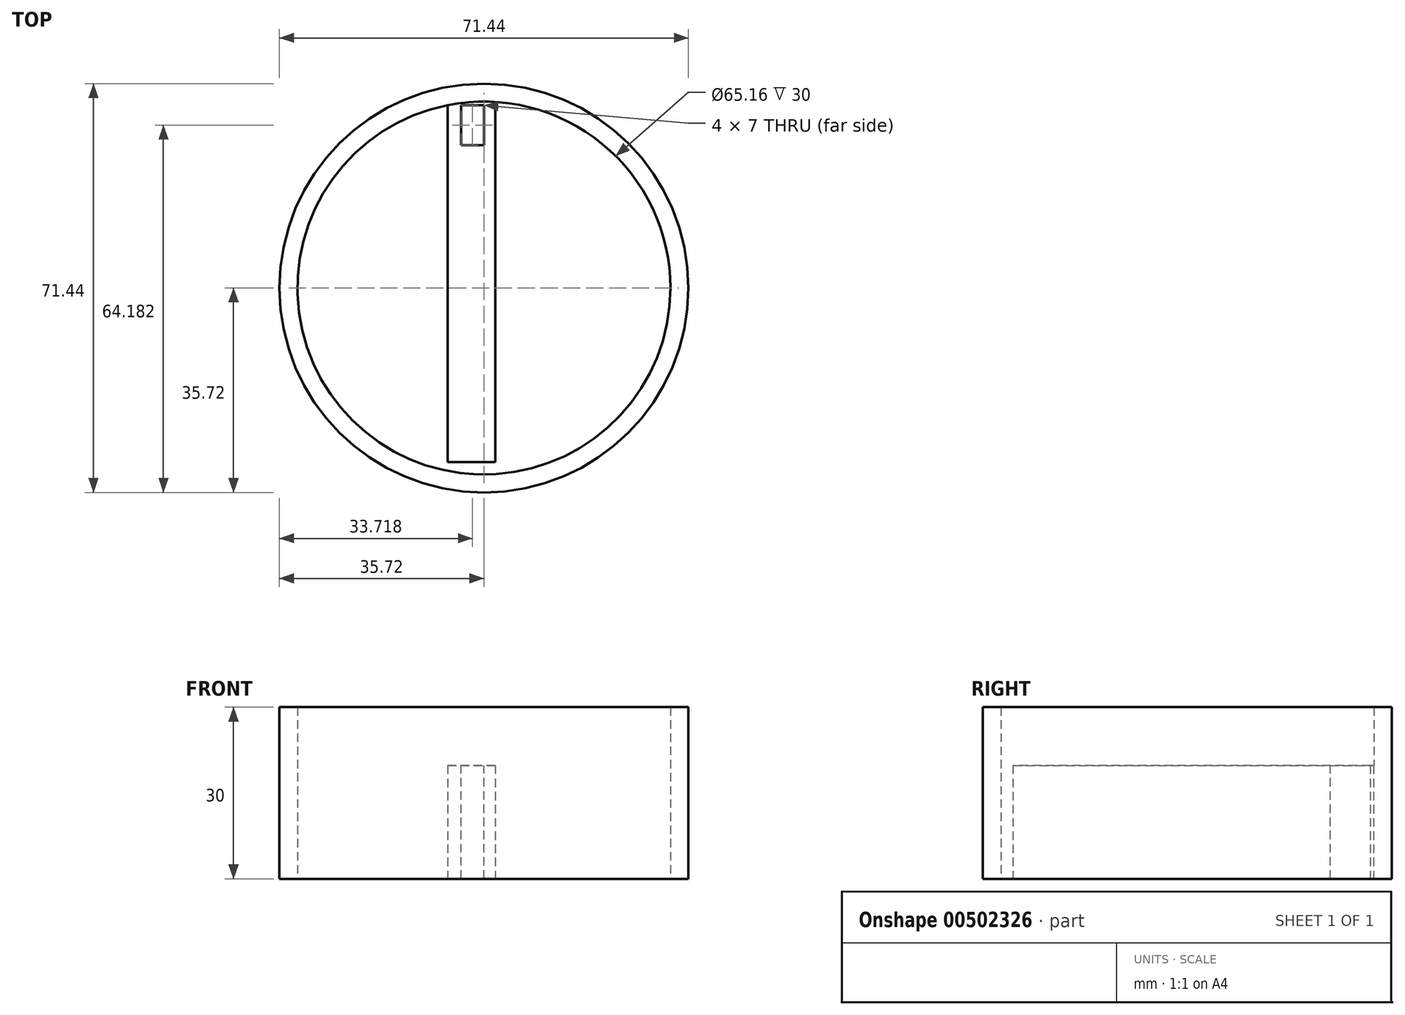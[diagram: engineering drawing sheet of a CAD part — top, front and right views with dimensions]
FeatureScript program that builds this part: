
annotation { "Feature Type Name" : "Feature", "Feature Type Description" : "" }
export const myFeature = defineFeature(function(context is Context, id is Id, definition is map)
    precondition{}
    {
        {
            var Q0;
            Q0=qCreatedBy(makeId("Top.planeOp"),FACE);
            var sketch = newSketch(context, id + "F0", { "sketchPlane" : qUnion([Q0])});
            skCircle(sketch, "E0", {"center": v(0, 0) * mm, "radius": 35.72 * mm});
            skSolve(sketch);
        }
        {
            var Q0;
            Q0=makeQuery(id+"F0.imprint","IMPRINT",FACE,{"disambiguationData":[TD([[makeQuery(id+"F0.imprint","IMPRINT",EDGE,{"derivedFrom":sQuery(id+"F0.wireOp",EDGE,"E0")}),1.0]])]});
            extrude(context, id + "F1", {"entities" : qUnion([Q0]), "depth" : 30 * mm});
        }
        {
            var Q0;
            Q0=makeQuery(id+"F1.opExtrude","CAP_FACE",FACE,{"disambiguationData":[OSD([sQuery(id+"F0.wireOp",EDGE,"E0")])],"isStart":true});
            var sketch = newSketch(context, id + "F2", { "sketchPlane" : qUnion([Q0])});
            skCircle(sketch, "E1", {"center": v(0, 0) * mm, "radius": 32.58 * mm});
            skSolve(sketch);
        }
        {
            var Q0;
            Q0=makeQuery(id+"F2.imprint","IMPRINT",FACE,{"disambiguationData":[TD([[makeQuery(id+"F2.imprint","IMPRINT",EDGE,{"derivedFrom":sQuery(id+"F2.wireOp",EDGE,"E1")}),1.0]])]});
            extrude(context, id + "F3", {"entities" : qUnion([Q0]), "operationType" : NewBodyOperationType.REMOVE, "oppositeDirection" : true, "depth" : 149 * mm});
        }
        {
            var Q0;
            Q0=qCreatedBy(makeId("Top.planeOp"),FACE);
            var sketch = newSketch(context, id + "F4", { "sketchPlane" : qUnion([Q0])});
            skLineSegment(sketch, "E2", {"start": v(-6.3, 34.13) * mm, "end": v(-6.3, -30.44) * mm});
            skLineSegment(sketch, "E3", {"start": v(-6.3, -30.44) * mm, "end": v(1.97, -30.44) * mm});
            skLineSegment(sketch, "E4", {"start": v(1.97, -30.44) * mm, "end": v(1.97, 35) * mm});
            skLineSegment(sketch, "E5", {"start": v(1.97, 35) * mm, "end": v(-6.3, 34.13) * mm});
            skSolve(sketch);
        }
        {
            var Q0;
            Q0=makeQuery(id+"F4.imprint","IMPRINT",FACE,{"disambiguationData":[TD([[makeQuery(id+"F4.imprint","IMPRINT",EDGE,{"derivedFrom":sQuery(id+"F4.wireOp",EDGE,"E2")}),1.0]])]});
            extrude(context, id + "F5", {"entities" : qUnion([Q0]), "operationType" : NewBodyOperationType.ADD, "depth" : 19.8 * mm});
        }
        {
            var Q0;
            Q0=makeQuery(id+"F5.opExtrude","CAP_FACE",FACE,{"disambiguationData":[OSD([sQuery(id+"F4.wireOp",EDGE,"E2"),sQuery(id+"F4.wireOp",EDGE,"E3"),sQuery(id+"F4.wireOp",EDGE,"E4"),sQuery(id+"F4.wireOp",EDGE,"E5")])],"isStart":false});
            var sketch = newSketch(context, id + "F6", { "sketchPlane" : qUnion([Q0])});
            skLineSegment(sketch, "E6", {"start": v(-4, 24.96) * mm, "end": v(0, 24.96) * mm});
            skLineSegment(sketch, "E7", {"start": v(0, 24.96) * mm, "end": v(0, 31.96) * mm});
            skLineSegment(sketch, "E8", {"start": v(-4, 24.96) * mm, "end": v(-4, 31.96) * mm});
            skLineSegment(sketch, "E9", {"start": v(-4, 31.96) * mm, "end": v(0, 31.96) * mm});
            skSolve(sketch);
        }
        {
            var Q0;
            Q0=makeQuery(id+"F6.imprint","IMPRINT",FACE,{"disambiguationData":[TD([[makeQuery(id+"F6.imprint","IMPRINT",EDGE,{"derivedFrom":sQuery(id+"F6.wireOp",EDGE,"E6")}),1.0]])]});
            extrude(context, id + "F7", {"entities" : qUnion([Q0]), "operationType" : NewBodyOperationType.REMOVE, "oppositeDirection" : true, "depth" : 120.5 * mm});
        }
    });
